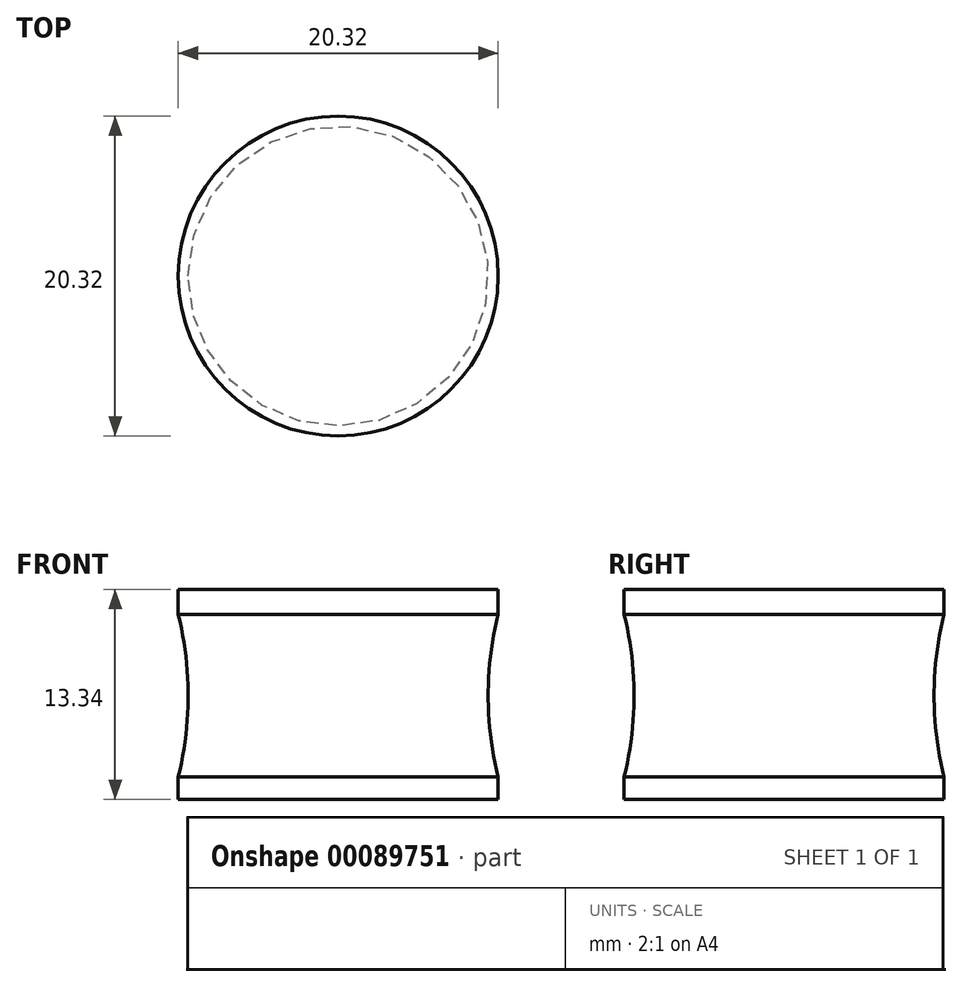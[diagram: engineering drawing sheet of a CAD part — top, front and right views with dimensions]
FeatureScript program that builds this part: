
annotation { "Feature Type Name" : "Feature", "Feature Type Description" : "" }
export const myFeature = defineFeature(function(context is Context, id is Id, definition is map)
    precondition{}
    {
        {
            var Q0;
            Q0=qCreatedBy(makeId("Top.planeOp"),FACE);
            var sketch = newSketch(context, id + "F0", { "sketchPlane" : qUnion([Q0])});
            skCircle(sketch, "E0", {"center": v(0, 0) * mm, "radius": 10.16 * mm});
            skSolve(sketch);
        }
        {
            var Q0;
            Q0=makeQuery(id+"F0.imprint","IMPRINT",FACE,{"disambiguationData":[TD([[makeQuery(id+"F0.imprint","IMPRINT",EDGE,{"derivedFrom":sQuery(id+"F0.wireOp",EDGE,"E0")}),1.0]])]});
            extrude(context, id + "F1", {"entities" : qUnion([Q0]), "depth" : 13.33 * mm});
        }
        {
            var Q0;
            Q0=qCreatedBy(makeId("Top.planeOp"),FACE);
            var sketch = newSketch(context, id + "F2", { "sketchPlane" : qUnion([Q0])});
            skText(sketch, "E1", { "text": "TY", "fontName": "OpenSans-Regular.ttf"});
            const initialGuessF2  = {"E1": [-0.0057, -0.00399, 1, 0, 0.00788]};
            skSetInitialGuess(sketch, initialGuessF2);
            skSolve(sketch);
        }
        {
            var Q0;
            Q0=qCreatedBy(makeId("Front.planeOp"),FACE);
            var sketch = newSketch(context, id + "F3", { "sketchPlane" : qUnion([Q0])});
            skCircle(sketch, "E2", {"center": v(-30.79, 6.6) * mm, "radius": 21.26 * mm});
            skLineSegment(sketch, "E3", {"start": v(-9.53, 17.52) * mm, "end": v(-9.53, -1.92) * mm, "construction": true});
            skSolve(sketch);
        }
        {
            var Q0;
            Q0=qCreatedBy(makeId("Front.planeOp"),FACE);
            var sketch = newSketch(context, id + "F4", { "sketchPlane" : qUnion([Q0])});
            skLineSegment(sketch, "E4", {"start": v(0, 32.61) * mm, "end": v(0, -18.4) * mm});
            skSolve(sketch);
        }
        {
            var Q0;
            Q0=makeQuery(id+"F3.imprint","IMPRINT",FACE,{"disambiguationData":[TD([[makeQuery(id+"F3.imprint","IMPRINT",EDGE,{"derivedFrom":sQuery(id+"F3.wireOp",EDGE,"E2")}),1.0]])]});
            var Q1;
            Q1=sQuery(id+"F4.wireOp",EDGE,"E4");
            revolve(context, id + "F5", {"operationType" : NewBodyOperationType.REMOVE, "entities" : qUnion([Q0]), "axis" : qUnion([Q1]), "revolveType" : RevolveType.FULL, "oppositeDirection" : true});
        }
    });
